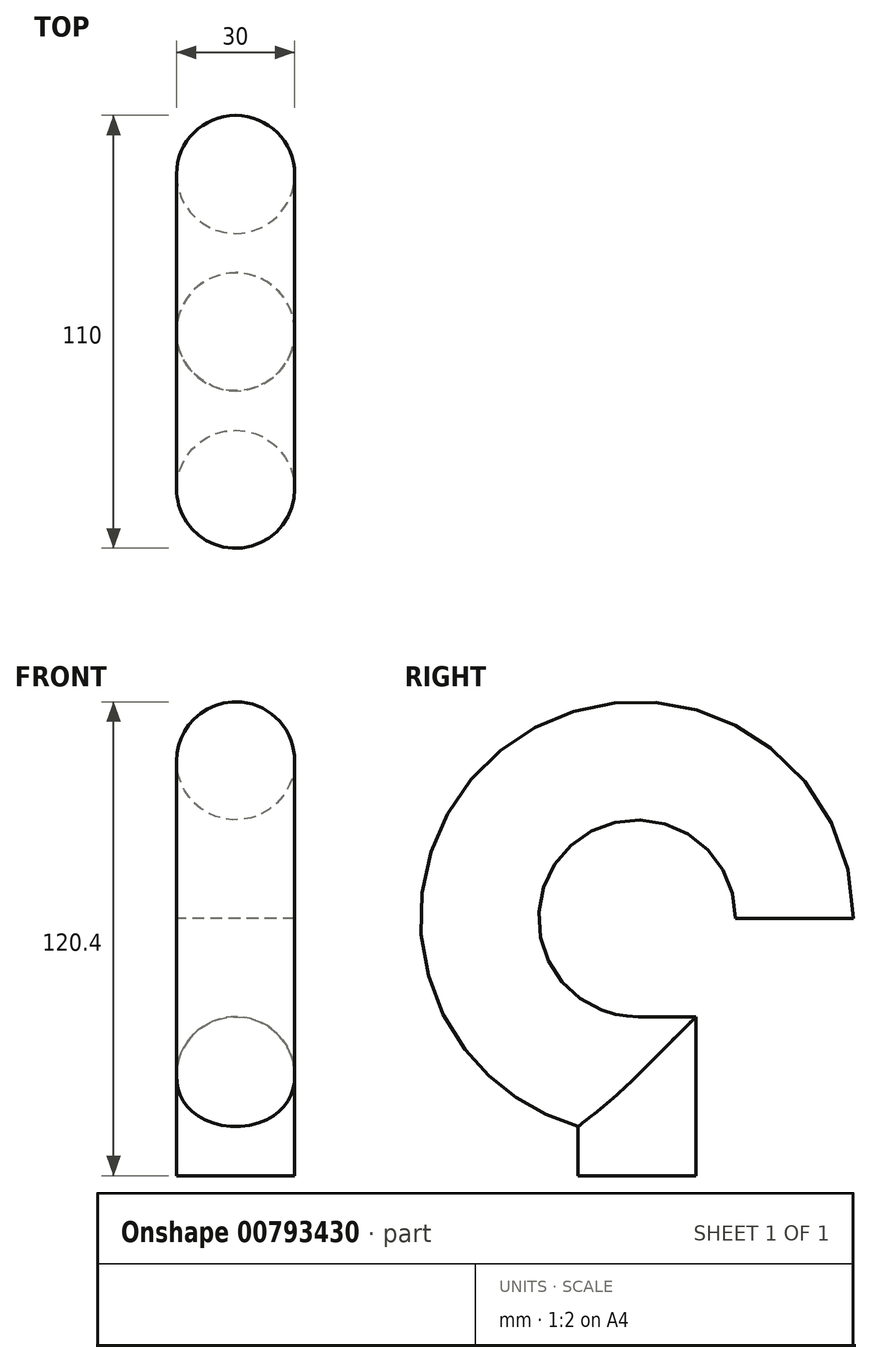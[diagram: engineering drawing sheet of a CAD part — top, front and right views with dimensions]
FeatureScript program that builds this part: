
annotation { "Feature Type Name" : "Feature", "Feature Type Description" : "" }
export const myFeature = defineFeature(function(context is Context, id is Id, definition is map)
    precondition{}
    {
        {
            var Q0;
            Q0=qCreatedBy(makeId("Right.planeOp"),FACE);
            var sketch = newSketch(context, id + "F0", { "sketchPlane" : qUnion([Q0])});
            skLineSegment(sketch, "E0", {"start": v(0, -40) * mm, "end": v(0, -65.4) * mm});
            skArc(sketch, "E1", {"start": v(40, 0) * mm, "mid": v(-28.28, 28.28) * mm, "end": v(0, -40) * mm});
            skSolve(sketch);
        }
        {
            var Q0;
            Q0=qCreatedBy(makeId("Top.planeOp"),FACE);
            var sketch = newSketch(context, id + "F1", { "sketchPlane" : qUnion([Q0])});
            skCircle(sketch, "E2", {"center": v(0, 40) * mm, "radius": 15 * mm});
            skSolve(sketch);
        }
        {
            var Q0;
            Q0=makeQuery(id+"F1.imprint","IMPRINT",FACE,{"disambiguationData":[TD([[makeQuery(id+"F1.imprint","IMPRINT",EDGE,{"derivedFrom":sQuery(id+"F1.wireOp",EDGE,"E2")}),1.0]])]});
            var Q1;
            Q1=sQuery(id+"F0.wireOp",EDGE,"E1");
            var Q2;
            Q2=sQuery(id+"F0.wireOp",EDGE,"E0");
            sweep(context, id + "F2", {"profiles" : qUnion([Q0]), "path" : qUnion([Q1, Q2])});
        }
    });
